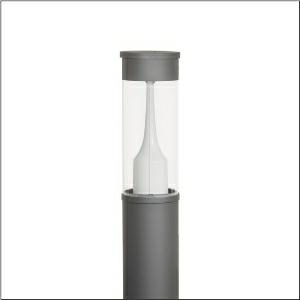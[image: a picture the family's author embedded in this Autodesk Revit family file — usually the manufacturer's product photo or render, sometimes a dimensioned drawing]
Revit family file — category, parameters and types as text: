
# Revit family: city-light_260_iq___p1_0a_5xa5295lf14h_3d8e
name_source: partatom
category: Lighting Fixtures
units: mm (PartAtom-declared; Revit-internal decimal feet)

## family parameters
Cut with Voids When Loaded = No
Host = Face
Light Source = No
Part Type = Normal
Room Calculation Point = No
Round Connector Dimension = Use Diameter
Shared = No

## types (1)
- --- (1 x LED, 1510 lm, 10 W, 4000K)
    Apparent Load = 10 VA
    CIE Flux Codes = 32 61 90 93 100
    Color Rendering = 70
    Color Temperature = 4000K
    Default Elevation = 1800 mm
    Description = City-Light 260 iQ, light pillar, Module 540 iQ-SR, primary light control with 3 zone facetted reflector, of plastic, silver coated, highly specular, structured, primary optical cover: cover, of PMMA, transparent, partly coated, light distribution: P1.0a, primary light characteristic: strongly asymmetric, LED, High Power LED, rated luminous flux: 1.510lm, luminous efficacy: 151lm/W, light colour: 740, colour temperature: 4000K, control gear: iQ Street-Remote, control: pre-setting: logarithmic dimming characteristic, Street-Remote, Auto-Match, Temp-Guard, Lumen-Switch, Night-Set, Smart-Wire, Light-Fading, Desk-Remote (wireless, voltage-free reading and setting of iQ features in the workshop via application-optimized NFC function/RFID function), optimised constant luminous flux control (CLO 2.0), with terminal, 6-pole, max. 2.5mm², mains connection: 230..240V, AC, 50/60Hz, start of lifetime: 10W, end of service life: 10W, reduction: 5W, luminaire housing, cylindrical, of extruded aluminium section, coated, Siteco® metallic grey (DB 702S), length: 2.600mm, diameter: 200mm, Module 540 iQ-SR, traffic white (RAL 9016), equipment: standard, protection rating (complete): IP65, insulation class (complete): insulation class II (safety insulation), certification: CE, ENEC, VDE, packaging unit: 1 piece

Light Distribution: P1.0a
    Height = 500 mm
    Lamp = 1 x LED
    Lamp Light Flux = 1510 lm
    Lamp Power = 10 W
    Lamp count = 1
    Length = 200 mm  [stored 0.656168 ft]
    Luminous efficacy = 151 lm/W
    Manufacturer = Siteco
    ModVariant = No
    Model = 5XA5295LF14H
    Mounting Place = Floor
    Mounting Type = Freestanding
    Number of Poles = 1
    OnlyDefault = Yes
    Power Factor = 1
    Product Name = City-Light 260 iQ | P1.0a
    Product group = light pillar
    ProductGroupID = 1301
    Protection Class = Protection class II
    Protection Degree = IP 65
    RLX_Detail_Level = 1
    RLX_Emergency_Light_Flux = 0 lm
    RLX_Emergency_Type = 0
    RLX_Emergency_Type_DB = No
    RlxData = <blob elided: 56961 chars, md5=ca01c8c4>
    Socket = socket
    Standby Power = 0 W
    System Light Flux = 1510 lm
    System Power = 10 W
    Type Comments = factory setting: luminous flux: 100 % | dim-lin: 254 | 401 mA
    Type Image = l_1006918.jpg
    URL = http://relux.com
    VarID = @adj_158943
    Voltage = 0 V
    Weight = 0.00 kg
    Width = 0 mm  [stored 0 ft]

note: [stored X ft] marks values corroborated as IEEE doubles in the binary element streams (Revit-internal decimal feet)

## geometry (parser evidence)
native form markers: Blend x4, Sweep x13
no freeform markers — native parametric forms only
